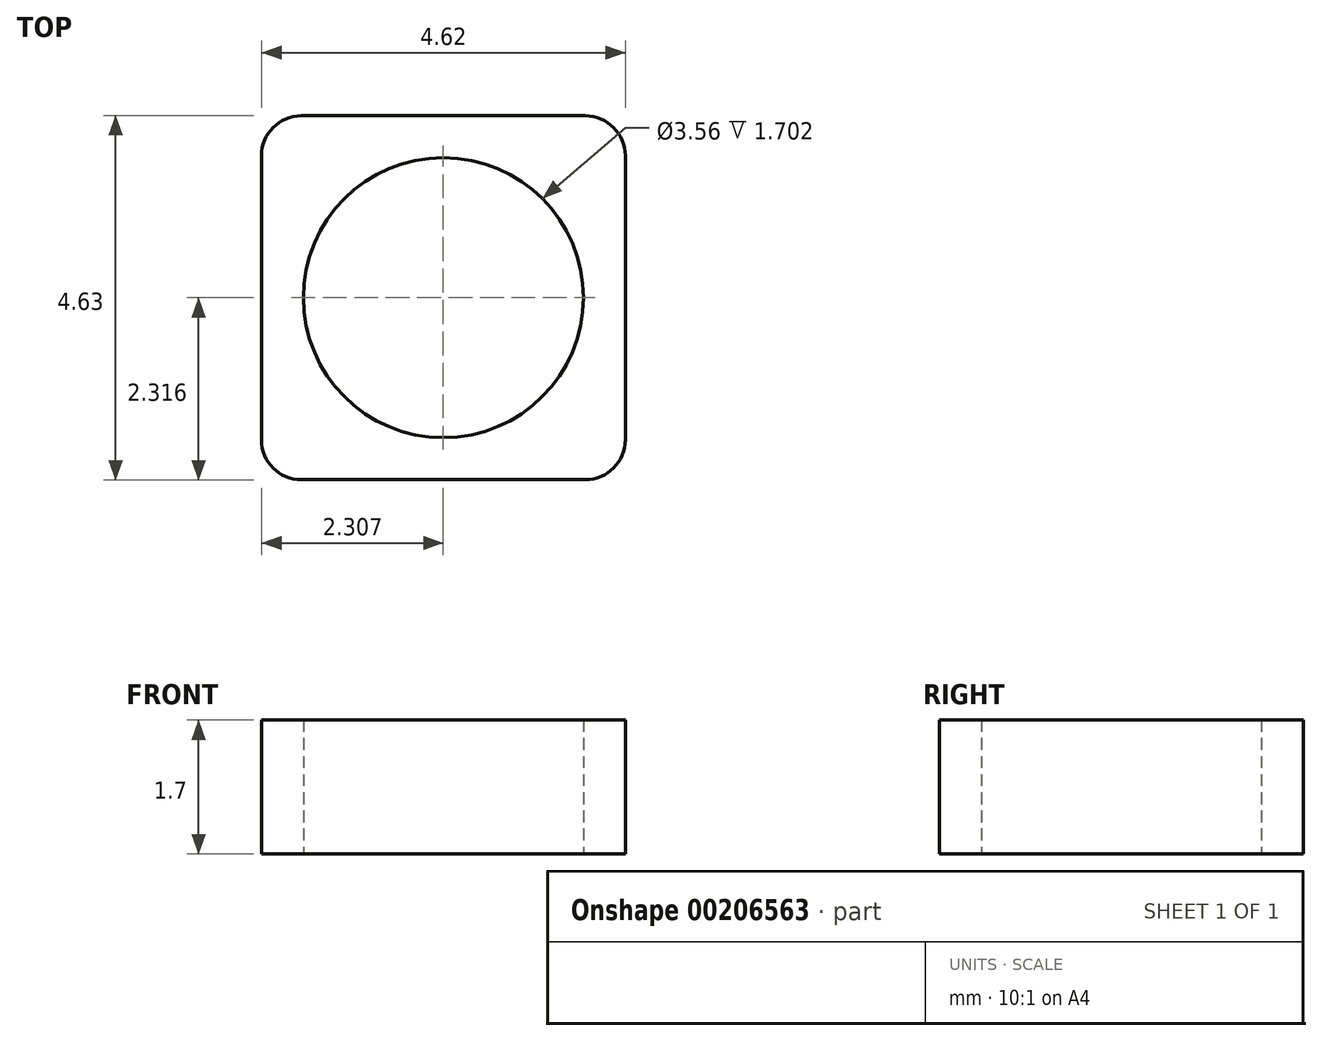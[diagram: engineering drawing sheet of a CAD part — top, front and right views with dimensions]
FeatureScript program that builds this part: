
annotation { "Feature Type Name" : "Feature", "Feature Type Description" : "" }
export const myFeature = defineFeature(function(context is Context, id is Id, definition is map)
    precondition{}
    {
        {
            var Q0;
            Q0=qCreatedBy(makeId("Top.planeOp"),FACE);
            var sketch = newSketch(context, id + "F0", { "sketchPlane" : qUnion([Q0])});
            skLineSegment(sketch, "E0.bottom", {"start": v(-1.42, -2.06) * mm, "end": v(2.2, -2.06) * mm});
            skLineSegment(sketch, "E0.top", {"start": v(-1.42, -6.69) * mm, "end": v(2.2, -6.69) * mm});
            skLineSegment(sketch, "E0.left", {"start": v(-1.92, -2.57) * mm, "end": v(-1.92, -6.18) * mm});
            skLineSegment(sketch, "E0.right", {"start": v(2.7, -2.57) * mm, "end": v(2.7, -6.18) * mm});
            skPoint(sketch, "E1.visualSharp", {"position": v(-1.92, -2.06) * mm});
            skArc(sketch, "E1.filletArc", {"start": v(-1.42, -2.06) * mm, "mid": v(-1.78, -2.21) * mm, "end": v(-1.92, -2.57) * mm});
            skPoint(sketch, "E2.visualSharp", {"position": v(2.7, -2.06) * mm});
            skArc(sketch, "E2.filletArc", {"start": v(2.7, -2.57) * mm, "mid": v(2.55, -2.21) * mm, "end": v(2.2, -2.06) * mm});
            skPoint(sketch, "E3.visualSharp", {"position": v(2.7, -6.69) * mm});
            skArc(sketch, "E3.filletArc", {"start": v(2.2, -6.69) * mm, "mid": v(2.55, -6.54) * mm, "end": v(2.7, -6.18) * mm});
            skPoint(sketch, "E4.visualSharp", {"position": v(-1.92, -6.69) * mm});
            skArc(sketch, "E4.filletArc", {"start": v(-1.92, -6.18) * mm, "mid": v(-1.78, -6.54) * mm, "end": v(-1.42, -6.69) * mm});
            skLineSegment(sketch, "E5", {"start": v(0.39, -2.06) * mm, "end": v(0.39, -6.69) * mm, "construction": true});
            skLineSegment(sketch, "E6", {"start": v(-1.92, -4.37) * mm, "end": v(2.7, -4.37) * mm, "construction": true});
            skSolve(sketch);
        }
        {
            var Q0;
            Q0=makeQuery(id+"F0.imprint","IMPRINT",FACE,{"disambiguationData":[TD([[makeQuery(id+"F0.imprint","IMPRINT",EDGE,{"derivedFrom":sQuery(id+"F0.wireOp",EDGE,"pmr4aMlz-oK6e-otBG-mzZ8-1n1HZyh7NjUq")}),1.0]])]});
            var Q1;
            Q1=makeQuery(id+"F0.imprint","IMPRINT",FACE,{"disambiguationData":[TD([[makeQuery(id+"F0.imprint","IMPRINT",EDGE,{"derivedFrom":sQuery(id+"F0.wireOp",EDGE,"E0.bottom")}),-1.0]])]});
            extrude(context, id + "F1", {"entities" : qUnion([Q0, Q1]), "depth" : 1.7 * mm});
        }
        {
            var Q0;
            Q0=makeQuery(id+"F1.opExtrude","CAP_FACE",FACE,{"disambiguationData":[OSD([sQuery(id+"F0.wireOp",EDGE,"E0.bottom"),sQuery(id+"F0.wireOp",EDGE,"E0.top"),sQuery(id+"F0.wireOp",EDGE,"E0.left"),sQuery(id+"F0.wireOp",EDGE,"E0.right"),sQuery(id+"F0.wireOp",EDGE,"E1.filletArc"),sQuery(id+"F0.wireOp",EDGE,"E2.filletArc"),sQuery(id+"F0.wireOp",EDGE,"E3.filletArc"),sQuery(id+"F0.wireOp",EDGE,"E4.filletArc")])],"isStart":true});
            var sketch = newSketch(context, id + "F2", { "sketchPlane" : qUnion([Q0])});
            skLineSegment(sketch, "E7", {"start": v(0.39, 7.55) * mm, "end": v(0.39, 0.16) * mm, "construction": true});
            skPoint(sketch, "E7.startSnap0", {"position": v(0.39, 6.69) * mm});
            skLineSegment(sketch, "E8", {"start": v(-2.2, 4.37) * mm, "end": v(4.27, 4.37) * mm, "construction": true});
            skPoint(sketch, "E8.startSnap0", {"position": v(-1.92, 4.37) * mm});
            skCircle(sketch, "E9", {"center": v(0.39, 4.37) * mm, "radius": 1.78 * mm});
            skSolve(sketch);
        }
        {
            var Q0;
            Q0=sQuery(id+"F2.wireOp",VERTEX,"Y2sMZet2-zUFK-2XUI-GhAY-nZ9tLXVwpEcH.center");
            var Q1;
            Q1=sQuery(id+"F2.wireOp",VERTEX,"E9.center");
            var Q2;
            Q2=makeQuery(id+"F1.opExtrude","SWEPT_BODY",BODY,{"disambiguationData":[OSD([sQuery(id+"F0.wireOp",EDGE,"E0.bottom"),sQuery(id+"F0.wireOp",EDGE,"E0.top"),sQuery(id+"F0.wireOp",EDGE,"E0.left"),sQuery(id+"F0.wireOp",EDGE,"E0.right"),sQuery(id+"F0.wireOp",EDGE,"E1.filletArc"),sQuery(id+"F0.wireOp",EDGE,"E2.filletArc"),sQuery(id+"F0.wireOp",EDGE,"E3.filletArc"),sQuery(id+"F0.wireOp",EDGE,"E4.filletArc")])]});
            hole(context, id + "F3", {"style" : HoleStyle.SIMPLE, "endStyle" : HoleEndStyle.THROUGH, "holeDiameter" : 3.56 * mm, "locations" : qUnion([Q0, Q1]), "scope" : qUnion([Q2]), "isTappedThrough" : true});
        }
    });
